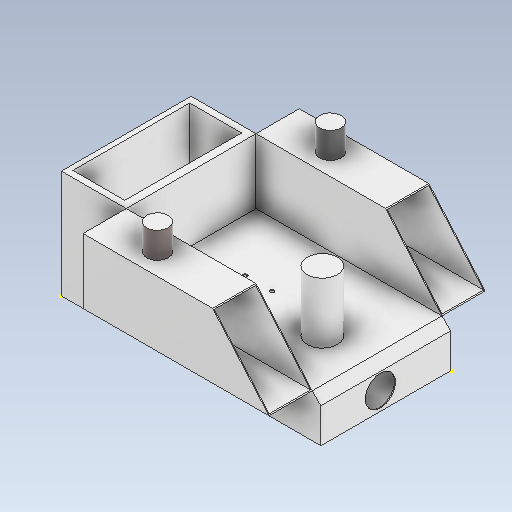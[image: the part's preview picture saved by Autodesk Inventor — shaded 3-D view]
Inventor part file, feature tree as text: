
AUTODESK INVENTOR PART (.ipt)
format: ipt  version: 2021 (Build 250183000, 183)  size: 255,488 bytes
history: native  units: mm
features: sketch x18, extrude x9, chamfer x1, shell x1, plane x1
ambient origin geometry x8: Origin, YZ Plane, XZ Plane, XY Plane, X Axis, Y Axis, Z Axis, Center Point
bodies: Solid1 (feature_tree)
feature tree (30):
  extrude  "Extrusion1"  Depth=50.0mm
  extrude  "Extrusion2"  Depth=75.0mm
  sketch  "Sketch3"  dims[d5=60.0mm]
  chamfer  "Chamfer1"  Distance=75.0mm
  sketch  "Sketch5"  dims[d6=135.0mm]
  extrude  "Extrusion4"  Depth=50.0mm TaperAngle=0.0deg
  sketch  "Sketch7"  dims[d10=10.0mm d11=2.0mm d12=45.0deg d17=50.0mm d18=0.0mm]
  extrude  "Extrusion5"  Depth=1.0mm
  shell  "Shell1"  Thickness=25.0mm
  extrude  "Extrusion6"  Depth=30.0mm TaperAngle=0.0deg
  extrude  "Extrusion7"  Depth=70.0mm TaperAngle=0.0deg
  sketch  "Sketch11"  dims[d29=35.0mm d30=5.0mm d31=0.0mm]
  sketch  "Sketch12"  dims[d32=1.0mm d33=1.0mm]
  extrude  "Extrusion8"  Depth=5.0mm TaperAngle=0.0deg
  sketch  "Sketch14"  dims[d36=200.0mm d37=0.0mm]
  sketch  "Sketch15"  dims[d38=96.5mm]
  extrude  "Extrusion9"  Depth=1.0mm
  plane  "Work Plane1"
  extrude  "Extrusion11"  Depth=5.0mm
  sketch  "Sketch19"  dims[d52=10.0mm d53=0.0mm]
  sketch  "Sketch20"  dims[d39=0.75mm d40=0.375mm]
  sketch  "Sketch1"  dims[d0=300.0mm d1=50.0mm]
  sketch  "Sketch2"  dims[d2=150.0mm d3=0.0mm d4=75.0mm]
  sketch  "Sketch6"  dims[d7=7.35mm d8=75.0mm d9=0.0mm]
  sketch  "Sketch8"  dims[d19=50.0mm d20=0.0mm d21=1.0mm d22=25.0mm]
  sketch  "Sketch9"  dims[d23=25.0mm d24=30.0mm d25=0.0mm]
  sketch  "Sketch10"  dims[d26=35.0mm d27=70.0mm d28=0.0mm]
  sketch  "Sketch13"  dims[d34=4.835mm d35=5.0mm]
  sketch  "Sketch16"  dims[d44=5.0mm]
  sketch  "Sketch18"  dims[d45=5.0mm]
